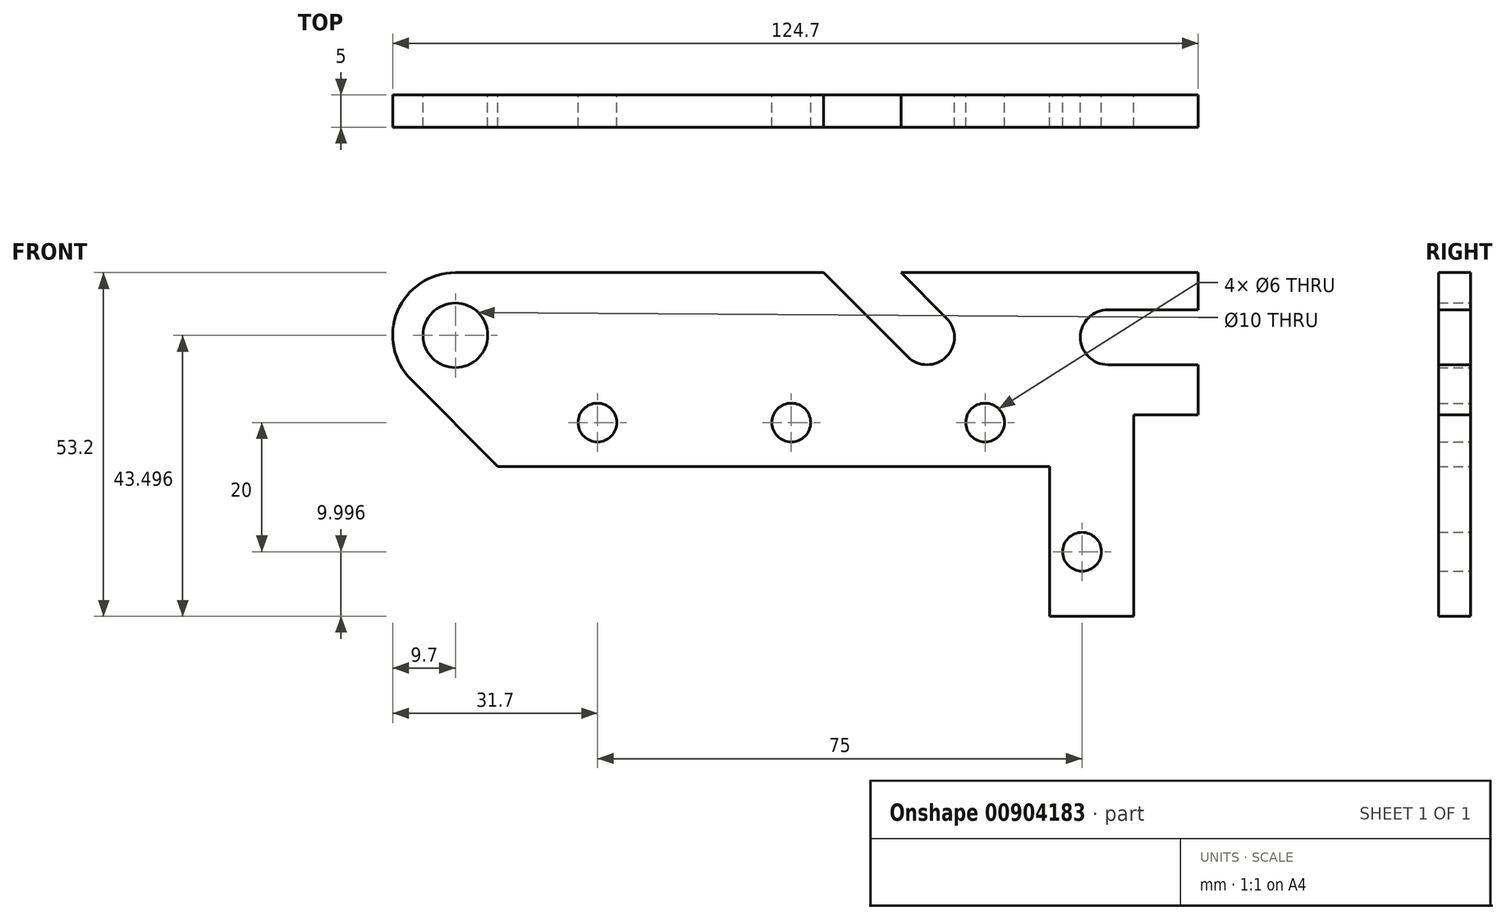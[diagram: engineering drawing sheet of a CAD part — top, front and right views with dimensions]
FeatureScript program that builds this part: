
annotation { "Feature Type Name" : "Feature", "Feature Type Description" : "" }
export const myFeature = defineFeature(function(context is Context, id is Id, definition is map)
    precondition{}
    {
        {
            var Q0;
            Q0=qCreatedBy(makeId("Front.planeOp"),FACE);
            var sketch = newSketch(context, id + "F0", { "sketchPlane" : qUnion([Q0])});
            skPoint(sketch, "E0", {"position": v(-63.18, 13.65) * mm});
            skLineSegment(sketch, "E1", {"start": v(-63.18, 23.65) * mm, "end": v(-6.2, 23.65) * mm});
            skLineSegment(sketch, "E2", {"start": v(51.82, 23.65) * mm, "end": v(51.82, 17.9) * mm});
            skPoint(sketch, "E3", {"position": v(18.82, 0.45) * mm});
            skPoint(sketch, "E4", {"position": v(-11.18, 0.45) * mm});
            skPoint(sketch, "E5", {"position": v(-41.18, 0.45) * mm});
            skLineSegment(sketch, "E6", {"start": v(28.82, -6.35) * mm, "end": v(-56.6, -6.35) * mm});
            skPoint(sketch, "E7", {"position": v(37.82, 13.65) * mm});
            skArc(sketch, "E8", {"start": v(37.82, 17.9) * mm, "mid": v(33.57, 13.65) * mm, "end": v(37.82, 9.4) * mm});
            skPoint(sketch, "E9", {"position": v(9.82, 13.65) * mm});
            skLineSegment(sketch, "E10", {"start": v(6.82, 10.64) * mm, "end": v(-6.2, 23.65) * mm});
            skLineSegment(sketch, "E11", {"start": v(37.82, 17.9) * mm, "end": v(51.82, 17.9) * mm});
            skLineSegment(sketch, "E12", {"start": v(37.82, 9.4) * mm, "end": v(51.82, 9.4) * mm});
            skPoint(sketch, "E13", {"position": v(51.82, 1.65) * mm});
            skLineSegment(sketch, "E14.bottom", {"start": v(51.82, 1.65) * mm, "end": v(41.82, 1.65) * mm});
            skLineSegment(sketch, "E15.trimOffspring", {"start": v(16.08, 23.65) * mm, "end": v(51.82, 23.65) * mm});
            skLineSegment(sketch, "E16.trimOffspring", {"start": v(51.82, 9.4) * mm, "end": v(51.82, 1.65) * mm});
            skPoint(sketch, "E17.orphan", {"position": v(0.38, 30.21) * mm});
            skArc(sketch, "E18", {"start": v(6.82, 10.64) * mm, "mid": v(12.83, 10.64) * mm, "end": v(12.83, 16.65) * mm});
            skLineSegment(sketch, "E19", {"start": v(12.83, 16.65) * mm, "end": v(5.83, 23.65) * mm});
            skLineSegment(sketch, "E20", {"start": v(5.83, 23.65) * mm, "end": v(16.65, 23.65) * mm});
            skLineSegment(sketch, "E21.top", {"start": v(41.82, -29.55) * mm, "end": v(28.82, -29.55) * mm});
            skLineSegment(sketch, "E21.right", {"start": v(28.82, -6.35) * mm, "end": v(28.82, -29.55) * mm});
            skPoint(sketch, "E22", {"position": v(33.82, -19.55) * mm});
            skCircle(sketch, "E23", {"center": v(33.82, -19.55) * mm, "radius": 3 * mm});
            skLineSegment(sketch, "E24", {"start": v(41.82, 1.65) * mm, "end": v(41.82, -29.55) * mm});
            skCircle(sketch, "E25", {"center": v(-41.18, 0.45) * mm, "radius": 3 * mm});
            skCircle(sketch, "E26", {"center": v(-11.18, 0.45) * mm, "radius": 3 * mm});
            skCircle(sketch, "E27", {"center": v(18.82, 0.45) * mm, "radius": 3 * mm});
            skPoint(sketch, "E28", {"position": v(-63.18, 13.95) * mm});
            skCircle(sketch, "E29", {"center": v(-63.18, 13.95) * mm, "radius": 5 * mm});
            skArc(sketch, "E30", {"start": v(-63.18, 23.65) * mm, "mid": v(-72.14, 17.66) * mm, "end": v(-70.04, 7.09) * mm});
            skLineSegment(sketch, "E31", {"start": v(-70.04, 7.09) * mm, "end": v(-56.6, -6.35) * mm});
            skSolve(sketch);
        }
        {
            var Q0;
            Q0=qSketchRegion(id+"F0",true);
            extrude(context, id + "F1", {"entities" : qUnion([Q0]), "depth" : 5 * mm, "offsetDistance" : 25 * mm});
        }
    });
